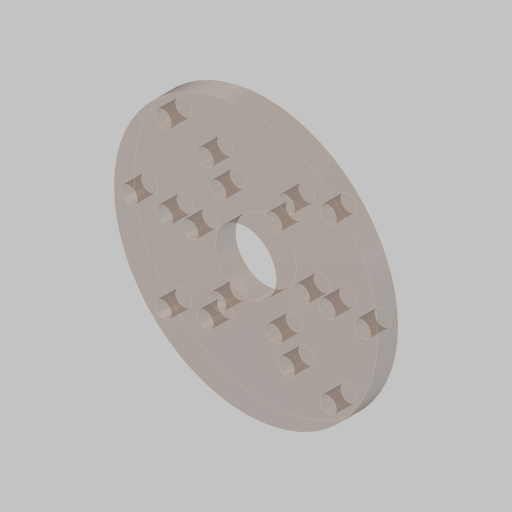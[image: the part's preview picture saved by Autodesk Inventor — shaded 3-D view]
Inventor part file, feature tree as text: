
AUTODESK INVENTOR PART (.ipt)
format: ipt  version: 2023.5 (Build 275446000, 446)  size: 322,048 bytes
history: native  units: in
note: dims shown in document units (in); Inventor stores cm internally (conversion verified against a paired STEP export)
features: sketch x1, extrude x1, hole x1
ambient origin geometry x8: Origin, YZ Plane, XZ Plane, XY Plane, X Axis, Y Axis, Z Axis, Center Point
bodies: Solid1 (feature_tree)
feature tree (3):
  sketch  "Sketch1"  dims[d0=0.75in d1=2.5in d2=0.375in d3=1.375in d8=0.25in d9=0.0in d18=2.0in d19=2.3622in d21=360.0deg d23=0.201in d24=0.75in d25=0.385in d26=0.25in d27=0.5635in d28=1.0in d29=0.8108in d30=45.0deg d31=1.5748in d33=360.0deg d35=1.5748in d37=360.0deg]
  extrude  "Extrusion1"  Depth=0.25in
  hole  "Hole2"  [1 undecoded]
note: 1 required parameter value undecoded (feature->parameter linkage not recoverable at this tier; creation-order binding heuristic only, values carry confidence <= 0.55)
